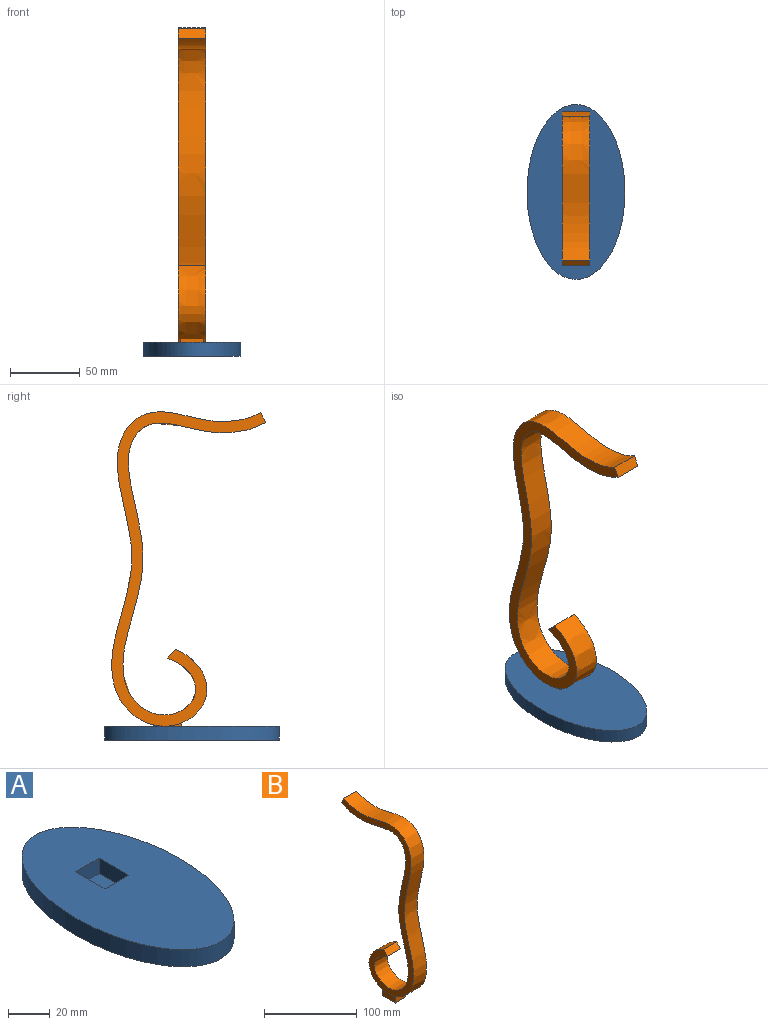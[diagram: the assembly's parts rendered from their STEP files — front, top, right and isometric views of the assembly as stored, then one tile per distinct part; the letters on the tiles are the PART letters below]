
ASSEMBLY  parts=2 mates=1
PART A: 8 faces, bbox 70x125x10 mm
  f0: plane 20x9mm, normal (1,0,0), area 180mm2, adj f1,f4,f5,f7
  f1: plane 16x9mm, normal (0,-1,0), area 144mm2, adj f0,f2,f5,f7
  f2: plane 20x9mm, normal (-1,0,0), area 180mm2, adj f1,f4,f5,f7
  f3: extruded ~125x70mm, area 3124.3mm2, adj f5,f6
  f4: plane 16x9mm, normal (0,1,0), area 144mm2, adj f0,f2,f5,f7
  f5: plane 125x70mm, normal (0,0,1), area 6552.2mm2, adj f0,f1,f2,f3,f4
  f6: plane 125x70mm, normal (0,0,-1), area 6872.2mm2, adj f3
  f7: plane 20x16mm, normal (0,0,1), area 320mm2, adj f0,f1,f2,f4
PART B: 11 faces, bbox 20x110x233.6 mm
  f0: plane 20x7.14mm, normal (0,0.89,0.45), area 160mm2, adj f1,f3,f4,f5
  f1: extruded ~224.42x106.29mm, area 8092.1mm2, adj f0,f2,f4,f5,f6,f7,f8,f9
  f2: plane 20x6.36mm, normal (0,-0.74,0.67), area 170.9mm2, adj f1,f3,f4,f5
  f3: extruded ~208.97x101.96mm, area 7623.6mm2, adj f0,f2,f4,f5
  f4: plane 224.66x110mm, normal (1,0,0), area 3211.1mm2, adj f0,f1,f2,f3
  f5: plane 224.66x110mm, normal (-1,0,0), area 3211.1mm2, adj f0,f1,f2,f3
  f6: plane 20.01x11.3mm, normal (-1,0,0), area 191.7mm2, adj f1,f7,f9,f10
  f7: plane 16x9.97mm, normal (0,-1,0), area 159.5mm2, adj f1,f6,f8,f10
  f8: plane 20.01x11.3mm, normal (1,0,0), area 191.7mm2, adj f1,f7,f9,f10
  f9: plane 16x11.29mm, normal (0,1,0), area 180.7mm2, adj f1,f6,f8,f10
  f10: plane 20x16mm, normal (0,0,-1), area 320mm2, adj f6,f7,f8,f9
PLACE A t=(89.01,264.79,47.13)mm
PLACE B rot(axis=(0,0,1),180deg) t=(99.01,282.29,105.83)mm
MATE fastened B.f10 <-> A.f7  axis (0,0,-1) through (89.01,282.29,48.13)mm
